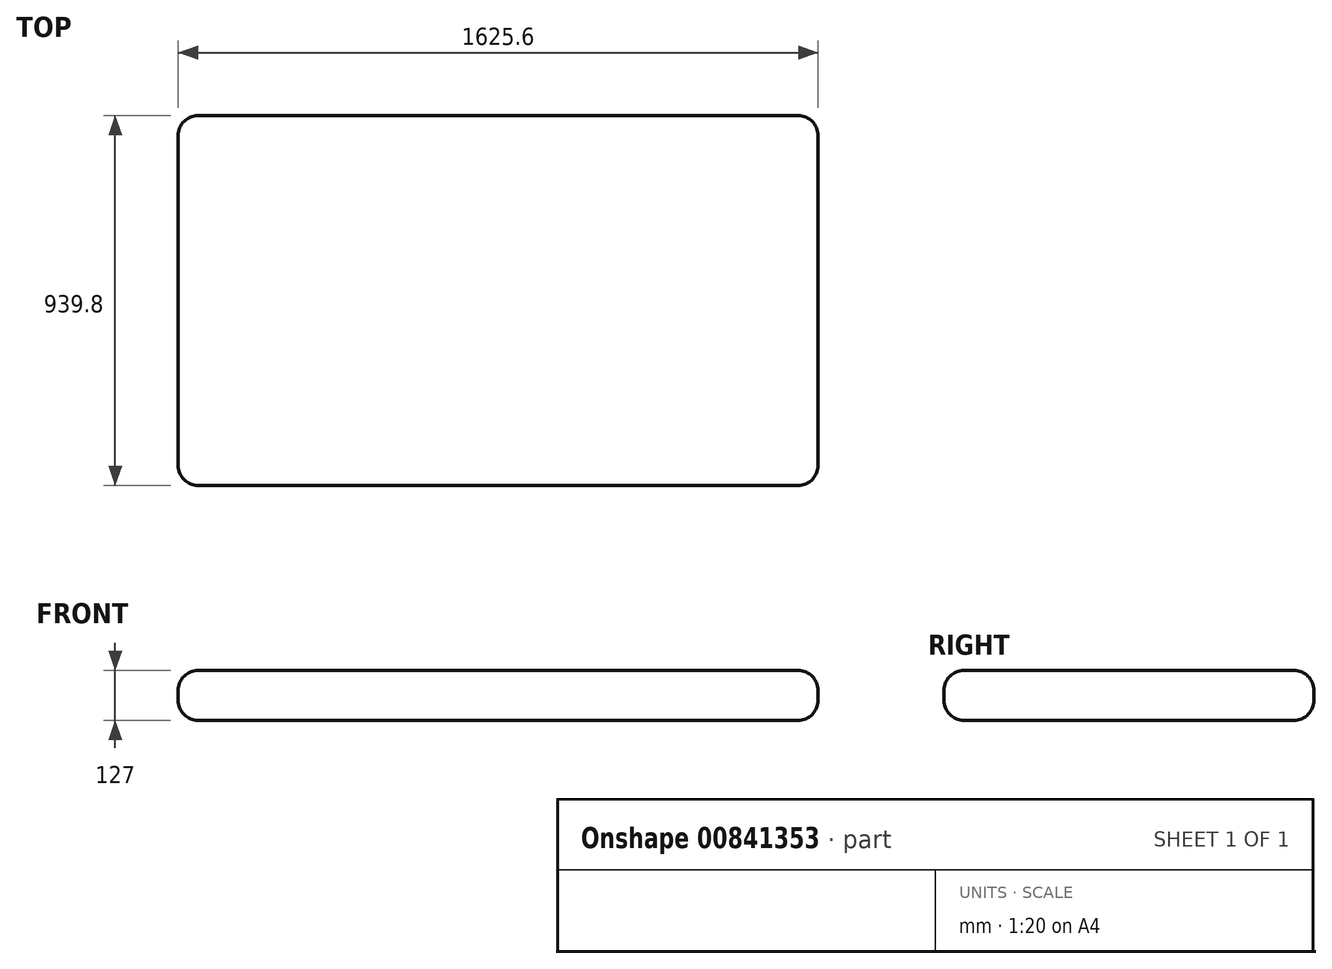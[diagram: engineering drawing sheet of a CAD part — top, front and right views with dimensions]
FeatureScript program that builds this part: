
annotation { "Feature Type Name" : "Feature", "Feature Type Description" : "" }
export const myFeature = defineFeature(function(context is Context, id is Id, definition is map)
    precondition{}
    {
        {
            var Q0;
            Q0=qCreatedBy(makeId("Top.planeOp"),FACE);
            var sketch = newSketch(context, id + "F0", { "sketchPlane" : qUnion([Q0])});
            skLineSegment(sketch, "E0.bottom", {"start": v(812.8, 317.5) * mm, "end": v(-812.8, 317.5) * mm});
            skLineSegment(sketch, "E0.top", {"start": v(812.8, -317.5) * mm, "end": v(-812.8, -317.5) * mm});
            skLineSegment(sketch, "E0.left", {"start": v(812.8, 317.5) * mm, "end": v(812.8, -317.5) * mm});
            skLineSegment(sketch, "E0.right", {"start": v(-812.8, 317.5) * mm, "end": v(-812.8, -317.5) * mm});
            skPoint(sketch, "E0.middle", {"position": v(0, 0) * mm});
            skSolve(sketch);
        }
        {
            var Q0;
            Q0 = qSketchRegion(id + "F0", true);
            extrude(context, id + "F1", {"entities" : qUnion([Q0]), "depth" : 127 * mm, "offsetDistance" : 25.4 * mm});
        }
        {
            var Q0;
            Q0=makeQuery(id+"F1.opExtrude","SWEPT_FACE",FACE,{"disambiguationData":[OSD([sQuery(id+"F0.wireOp",EDGE,"E0.top")])]});
            extrude(context, id + "F2", {"entities" : qUnion([Q0]), "operationType" : NewBodyOperationType.ADD, "depth" : 304.8 * mm, "offsetDistance" : 25.4 * mm});
        }
        {
            var Q0;
            {var subQ0=sQuery(id+"F0.wireOp",EDGE,"E0.top");Q0=makeQuery(id+"F2.boolean.opBoolean","MERGE",FACE,{"derivedFrom":[makeQuery(id+"F1.opExtrude","CAP_FACE",FACE,{"disambiguationData":[OSD([sQuery(id+"F0.wireOp",EDGE,"E0.bottom"),subQ0,sQuery(id+"F0.wireOp",EDGE,"E0.left"),sQuery(id+"F0.wireOp",EDGE,"E0.right")])],"isStart":false}),makeQuery(id+"F2.opExtrude","SWEPT_FACE",FACE,{"disambiguationData":[OSD([subQ0]),TDD([makeQuery(id+"F1.opExtrude","CAP_EDGE",EDGE,{"disambiguationData":[OSD([subQ0])],"isStart":false})])]})]});}
            var Q1;
            {var subQ0=sQuery(id+"F0.wireOp",EDGE,"E0.top");Q1=makeQuery(id+"F2.opExtrude","CAP_EDGE",EDGE,{"disambiguationData":[OSD([subQ0]),TDD([makeQuery(id+"F1.opExtrude","CAP_EDGE",EDGE,{"disambiguationData":[OSD([subQ0])],"isStart":true})])],"isStart":false});}
            var Q2;
            {var subQ0=sQuery(id+"F0.wireOp",EDGE,"E0.left");Q2=makeQuery(id+"F2.boolean.opBoolean","MERGE",FACE,{"derivedFrom":[makeQuery(id+"F1.opExtrude","SWEPT_FACE",FACE,{"disambiguationData":[OSD([subQ0])]}),makeQuery(id+"F2.opExtrude","SWEPT_FACE",FACE,{"disambiguationData":[OSD([sQuery(id+"F0.wireOp",EDGE,"E0.top"),subQ0])]})]});}
            var Q3;
            Q3=makeQuery(id+"F1.opExtrude","SWEPT_FACE",FACE,{"disambiguationData":[OSD([sQuery(id+"F0.wireOp",EDGE,"E0.bottom")])]});
            var Q4;
            {var subQ0=sQuery(id+"F0.wireOp",EDGE,"E0.right");Q4=makeQuery(id+"F2.boolean.opBoolean","MERGE",FACE,{"derivedFrom":[makeQuery(id+"F1.opExtrude","SWEPT_FACE",FACE,{"disambiguationData":[OSD([subQ0])]}),makeQuery(id+"F2.opExtrude","SWEPT_FACE",FACE,{"disambiguationData":[OSD([sQuery(id+"F0.wireOp",EDGE,"E0.top"),subQ0])]})]});}
            var Q5;
            {var subQ0=sQuery(id+"F0.wireOp",EDGE,"E0.top");Q5=makeQuery(id+"F2.boolean.opBoolean","MERGE",FACE,{"derivedFrom":[makeQuery(id+"F1.opExtrude","CAP_FACE",FACE,{"disambiguationData":[OSD([sQuery(id+"F0.wireOp",EDGE,"E0.bottom"),subQ0,sQuery(id+"F0.wireOp",EDGE,"E0.left"),sQuery(id+"F0.wireOp",EDGE,"E0.right")])],"isStart":true}),makeQuery(id+"F2.opExtrude","SWEPT_FACE",FACE,{"disambiguationData":[OSD([subQ0]),TDD([makeQuery(id+"F1.opExtrude","CAP_EDGE",EDGE,{"disambiguationData":[OSD([subQ0])],"isStart":true})])]})]});}
            fillet(context, id + "F3", {"entities" : qUnion([Q0, Q1, Q2, Q3, Q4, Q5]), "radius" : 50.8 * mm, "tangentPropagation" : true, "allowEdgeOverflow" : false});
        }
    });
